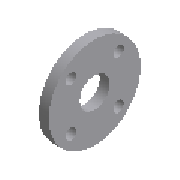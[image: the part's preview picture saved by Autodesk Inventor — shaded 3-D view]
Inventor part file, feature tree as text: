
AUTODESK INVENTOR PART (.ipt)
format: ipt  version: 2025.1 (Build 291241020, 241B)  size: 162,304 bytes
history: native  units: mm (DEFAULTED — no unit token found)
features: other x5, revolve x1, extrude x1, pattern_circular x1
ambient origin geometry x8: Origin, YZ Plane, XZ Plane, XY Plane, X Axis, Y Axis, Z Axis, Center Point
bodies: Solid1 (feature_tree)
feature tree (8):
  revolve  "Revolution1"  Angle=90.0deg
  extrude  "Extrusion1"  Depth=165.0mm
  pattern_circular  "Circular Pattern1"  [2 undecoded]
  other  "Work Axis1"
  other  "Work Point1"
  other  "Work Axis2"
  other  "Work Point2"
  other  "Work Point3"
note: 2 required parameter values undecoded (feature->parameter linkage not recoverable at this tier; creation-order binding heuristic only, values carry confidence <= 0.55)
